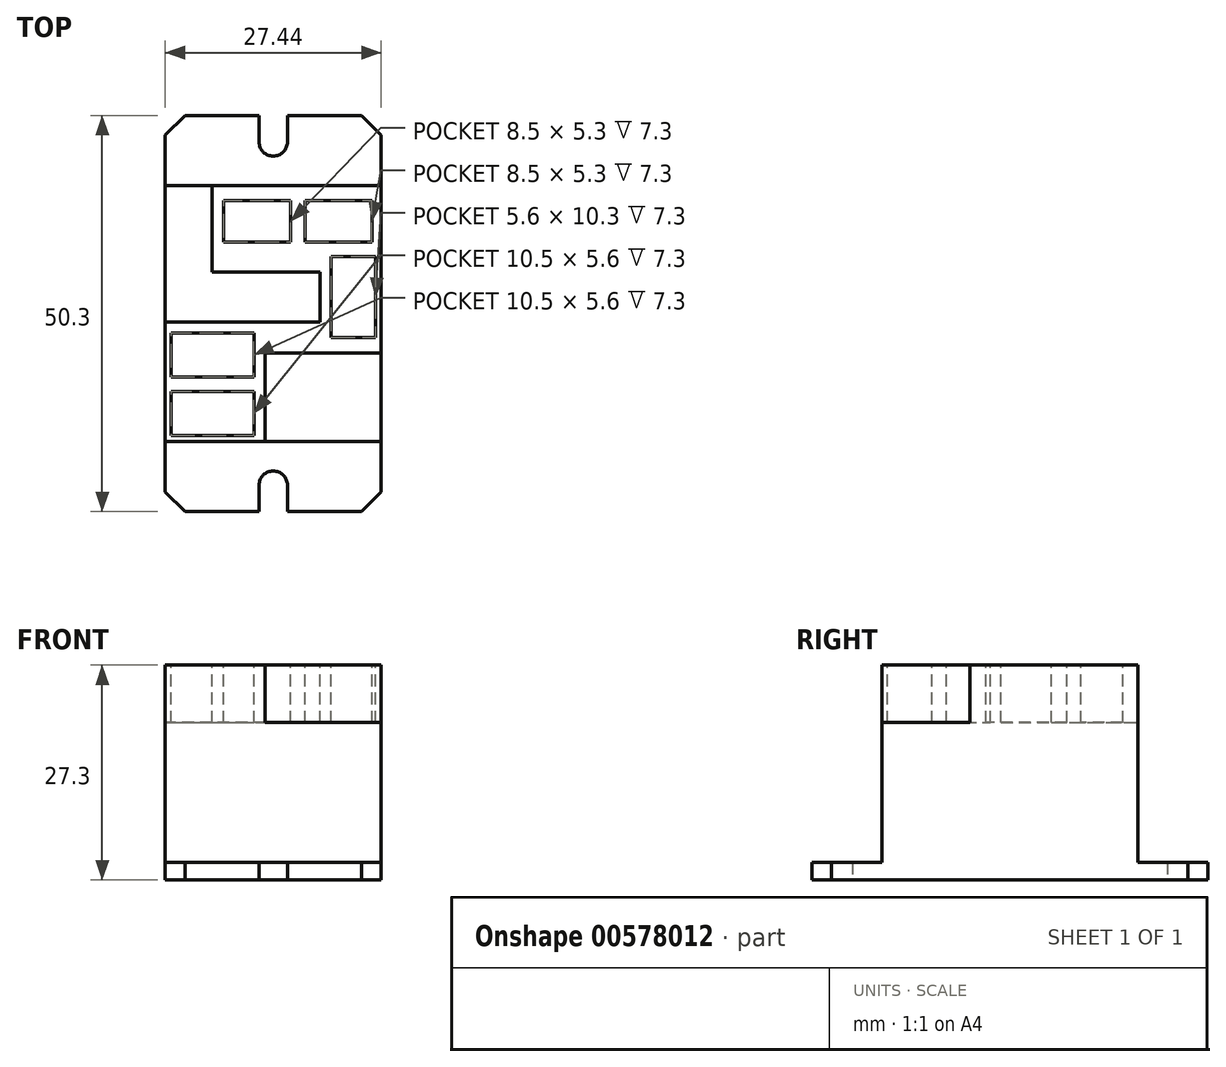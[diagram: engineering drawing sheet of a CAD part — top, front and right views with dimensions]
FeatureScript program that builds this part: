
annotation { "Feature Type Name" : "Feature", "Feature Type Description" : "" }
export const myFeature = defineFeature(function(context is Context, id is Id, definition is map)
    precondition{}
    {
        {
            var Q0;
            Q0=qCreatedBy(makeId("Top.planeOp"),FACE);
            var sketch = newSketch(context, id + "F0", { "sketchPlane" : qUnion([Q0])});
            skLineSegment(sketch, "E0.bottom", {"start": v(13.72, -25.15) * mm, "end": v(-13.72, -25.15) * mm});
            skLineSegment(sketch, "E0.top", {"start": v(13.72, 25.15) * mm, "end": v(-13.72, 25.15) * mm});
            skLineSegment(sketch, "E0.left", {"start": v(13.72, -25.15) * mm, "end": v(13.72, 25.15) * mm});
            skLineSegment(sketch, "E0.right", {"start": v(-13.72, -25.15) * mm, "end": v(-13.72, 25.15) * mm});
            skPoint(sketch, "E0.middle", {"position": v(0, 0) * mm});
            skLineSegment(sketch, "E1.bottom", {"start": v(13.72, -16.26) * mm, "end": v(-13.72, -16.26) * mm});
            skLineSegment(sketch, "E1.top", {"start": v(13.72, 16.26) * mm, "end": v(-13.72, 16.26) * mm});
            skLineSegment(sketch, "E1.left", {"start": v(13.72, -16.26) * mm, "end": v(13.72, 16.26) * mm});
            skLineSegment(sketch, "E1.right", {"start": v(-13.72, -16.26) * mm, "end": v(-13.72, 16.26) * mm});
            skSolve(sketch);
        }
        {
            var Q0;
            Q0=makeQuery(id+"F0.imprint","IMPRINT",FACE,{"disambiguationData":[TD([[makeQuery(id+"F0.imprint","IMPRINT",EDGE,{"derivedFrom":sQuery(id+"F0.wireOp",EDGE,"E1.bottom")}),-1.0]])]});
            extrude(context, id + "F1", {"entities" : qUnion([Q0]), "depth" : 27.3 * mm, "offsetDistance" : 25 * mm});
        }
        {
            var Q0;
            {var subQ0=sQuery(id+"F0.wireOp",EDGE,"E0.top");Q0=makeQuery(id+"F0.imprint","IMPRINT",FACE,{"disambiguationData":[TD([[makeQuery(id+"F0.imprint","IMPRINT",EDGE,{"derivedFrom":subQ0}),1.0]])]});}
            var Q1;
            {var subQ0=sQuery(id+"F0.wireOp",EDGE,"E0.bottom");Q1=makeQuery(id+"F0.imprint","IMPRINT",FACE,{"disambiguationData":[TD([[makeQuery(id+"F0.imprint","IMPRINT",EDGE,{"derivedFrom":subQ0}),-1.0]])]});}
            extrude(context, id + "F2", {"entities" : qUnion([Q0, Q1]), "operationType" : NewBodyOperationType.ADD, "depth" : 2.2 * mm, "offsetDistance" : 25 * mm});
        }
        {
            var Q0;
            Q0=makeQuery(id+"F2.opExtrude","SWEPT_EDGE",EDGE,{"disambiguationData":[OSD([sQuery(id+"F0.wireOp",EDGE,"E0.bottom"),sQuery(id+"F0.wireOp",EDGE,"E0.right")])]});
            var Q1;
            Q1=makeQuery(id+"F2.opExtrude","SWEPT_EDGE",EDGE,{"disambiguationData":[OSD([sQuery(id+"F0.wireOp",EDGE,"E0.bottom"),sQuery(id+"F0.wireOp",EDGE,"E0.left")])]});
            var Q2;
            Q2=makeQuery(id+"F2.opExtrude","SWEPT_EDGE",EDGE,{"disambiguationData":[OSD([sQuery(id+"F0.wireOp",EDGE,"E0.top"),sQuery(id+"F0.wireOp",EDGE,"E0.left")])]});
            var Q3;
            Q3=makeQuery(id+"F2.opExtrude","SWEPT_EDGE",EDGE,{"disambiguationData":[OSD([sQuery(id+"F0.wireOp",EDGE,"E0.top"),sQuery(id+"F0.wireOp",EDGE,"E0.right")])]});
            chamfer(context, id + "F3", {"entities" : qUnion([Q0, Q1, Q2, Q3]), "width" : 2.5 * mm, "tangentPropagation" : true});
        }
        {
            var Q0;
            Q0=makeQuery(id+"F1.opExtrude","CAP_FACE",FACE,{"disambiguationData":[OSD([sQuery(id+"F0.wireOp",EDGE,"E1.bottom"),sQuery(id+"F0.wireOp",EDGE,"E1.top"),sQuery(id+"F0.wireOp",EDGE,"E1.left"),sQuery(id+"F0.wireOp",EDGE,"E1.right")])],"isStart":false});
            var sketch = newSketch(context, id + "F4", { "sketchPlane" : qUnion([Q0])});
            skLineSegment(sketch, "E2.bottom", {"start": v(13.72, -16.26) * mm, "end": v(-1.02, -16.26) * mm});
            skLineSegment(sketch, "E2.top", {"start": v(13.72, -5.04) * mm, "end": v(-1.02, -5.04) * mm});
            skLineSegment(sketch, "E2.left", {"start": v(13.72, -16.26) * mm, "end": v(13.72, -5.04) * mm});
            skLineSegment(sketch, "E2.right", {"start": v(-1.02, -16.26) * mm, "end": v(-1.02, -5.04) * mm});
            skLineSegment(sketch, "E3", {"start": v(-13.72, 16.26) * mm, "end": v(-13.72, -1.1) * mm});
            skLineSegment(sketch, "E4", {"start": v(-13.72, -1.1) * mm, "end": v(5.92, -1.1) * mm});
            skLineSegment(sketch, "E5", {"start": v(5.92, -1.1) * mm, "end": v(5.92, 5.3) * mm});
            skLineSegment(sketch, "E6", {"start": v(5.92, 5.3) * mm, "end": v(-7.78, 5.3) * mm});
            skLineSegment(sketch, "E7", {"start": v(-7.78, 5.3) * mm, "end": v(-7.78, 16.26) * mm});
            skLineSegment(sketch, "E8", {"start": v(-7.78, 16.26) * mm, "end": v(-13.72, 16.26) * mm});
            skSolve(sketch);
        }
        {
            var Q0;
            Q0=makeQuery(id+"F4.imprint","IMPRINT",FACE,{"disambiguationData":[TD([[makeQuery(id+"F4.imprint","IMPRINT",EDGE,{"derivedFrom":sQuery(id+"F4.wireOp",EDGE,"E2.bottom")}),-1.0]])]});
            var Q1;
            Q1=makeQuery(id+"F4.imprint","IMPRINT",FACE,{"disambiguationData":[TD([[makeQuery(id+"F4.imprint","IMPRINT",EDGE,{"derivedFrom":sQuery(id+"F4.wireOp",EDGE,"E3")}),-1.0]])]});
            extrude(context, id + "F5", {"entities" : qUnion([Q0, Q1]), "operationType" : NewBodyOperationType.REMOVE, "oppositeDirection" : true, "depth" : 7.3 * mm, "offsetDistance" : 25 * mm});
        }
        {
            var Q0;
            Q0=makeQuery(id+"F1.opExtrude","CAP_FACE",FACE,{"disambiguationData":[OSD([sQuery(id+"F0.wireOp",EDGE,"E1.bottom"),sQuery(id+"F0.wireOp",EDGE,"E1.top"),sQuery(id+"F0.wireOp",EDGE,"E1.left"),sQuery(id+"F0.wireOp",EDGE,"E1.right")])],"isStart":false});
            var sketch = newSketch(context, id + "F6", { "sketchPlane" : qUnion([Q0])});
            skLineSegment(sketch, "E9", {"start": v(-7.78, 14.36) * mm, "end": v(13.72, 14.36) * mm, "construction": true});
            skLineSegment(sketch, "E10.bottom", {"start": v(-6.28, 14.36) * mm, "end": v(2.22, 14.36) * mm});
            skLineSegment(sketch, "E10.top", {"start": v(-6.28, 9.06) * mm, "end": v(2.22, 9.06) * mm});
            skLineSegment(sketch, "E10.left", {"start": v(-6.28, 14.36) * mm, "end": v(-6.28, 9.06) * mm});
            skLineSegment(sketch, "E10.right", {"start": v(2.22, 14.36) * mm, "end": v(2.22, 9.06) * mm});
            skLineSegment(sketch, "E11", {"start": v(3.12, 14.36) * mm, "end": v(3.12, 8.09) * mm, "construction": true});
            skLineSegment(sketch, "E12.MirrorCS", {"start": v(4.02, 14.36) * mm, "end": v(4.02, 9.06) * mm});
            skLineSegment(sketch, "E13.MirrorCS", {"start": v(12.52, 9.06) * mm, "end": v(4.02, 9.06) * mm});
            skLineSegment(sketch, "E14.MirrorCS", {"start": v(12.52, 14.36) * mm, "end": v(12.52, 9.06) * mm});
            skLineSegment(sketch, "E15", {"start": v(4.02, 14.36) * mm, "end": v(12.52, 14.36) * mm});
            skLineSegment(sketch, "E16", {"start": v(13.72, 7.26) * mm, "end": v(5.76, 7.26) * mm, "construction": true});
            skLineSegment(sketch, "E17", {"start": v(12.97, 7.26) * mm, "end": v(12.97, -5.04) * mm, "construction": true});
            skLineSegment(sketch, "E18.bottom", {"start": v(12.97, 7.26) * mm, "end": v(7.37, 7.26) * mm});
            skLineSegment(sketch, "E18.top", {"start": v(12.97, -3.04) * mm, "end": v(7.37, -3.04) * mm});
            skLineSegment(sketch, "E18.left", {"start": v(12.97, 7.26) * mm, "end": v(12.97, -3.04) * mm});
            skLineSegment(sketch, "E18.right", {"start": v(7.37, 7.26) * mm, "end": v(7.37, -3.04) * mm});
            skLineSegment(sketch, "E19", {"start": v(-12.97, -16.26) * mm, "end": v(-12.97, -1.1) * mm, "construction": true});
            skLineSegment(sketch, "E20", {"start": v(-12.97, -15.5) * mm, "end": v(-1.02, -15.5) * mm, "construction": true});
            skLineSegment(sketch, "E21.bottom", {"start": v(-12.97, -15.5) * mm, "end": v(-2.47, -15.5) * mm});
            skLineSegment(sketch, "E21.top", {"start": v(-12.97, -9.9) * mm, "end": v(-2.47, -9.9) * mm});
            skLineSegment(sketch, "E21.left", {"start": v(-12.97, -15.5) * mm, "end": v(-12.97, -9.9) * mm});
            skLineSegment(sketch, "E21.right", {"start": v(-2.47, -15.5) * mm, "end": v(-2.47, -9.9) * mm});
            skLineSegment(sketch, "E22.bottom", {"start": v(-12.97, -8.06) * mm, "end": v(-2.47, -8.06) * mm});
            skLineSegment(sketch, "E22.top", {"start": v(-12.97, -2.46) * mm, "end": v(-2.47, -2.46) * mm});
            skLineSegment(sketch, "E22.left", {"start": v(-12.97, -8.06) * mm, "end": v(-12.97, -2.46) * mm});
            skLineSegment(sketch, "E22.right", {"start": v(-2.47, -8.06) * mm, "end": v(-2.47, -2.46) * mm});
            skSolve(sketch);
        }
        {
            var Q0;
            Q0 = qSketchRegion(id + "F6", true);
            extrude(context, id + "F7", {"entities" : qUnion([Q0]), "operationType" : NewBodyOperationType.REMOVE, "oppositeDirection" : true, "depth" : 7.3 * mm, "offsetDistance" : 25 * mm});
        }
        {
            var Q0;
            Q0=makeQuery(id+"F0.imprint","IMPRINT",FACE,{"disambiguationData":[TD([[makeQuery(id+"F0.imprint","IMPRINT",EDGE,{"derivedFrom":sQuery(id+"F0.wireOp",EDGE,"E1.bottom")}),-1.0]])]});
            var sketch = newSketch(context, id + "F8", { "sketchPlane" : qUnion([Q0])});
            skPoint(sketch, "E23", {"position": v(0, -20) * mm});
            skPoint(sketch, "E24", {"position": v(0, 20) * mm});
            skLineSegment(sketch, "E25.bottom", {"start": v(0, -20) * mm, "end": v(0, -20) * mm});
            skLineSegment(sketch, "E25.top", {"start": v(0, -25.15) * mm, "end": v(-1.8, -25.15) * mm});
            skLineSegment(sketch, "E25.left", {"start": v(0, -20) * mm, "end": v(0, -25.15) * mm, "construction": true});
            skLineSegment(sketch, "E25.right", {"start": v(-1.8, -21.8) * mm, "end": v(-1.8, -25.15) * mm});
            skPoint(sketch, "E26.visualSharp", {"position": v(-1.8, -20) * mm});
            skArc(sketch, "E26.filletArc", {"start": v(0, -20) * mm, "mid": v(-1.27, -20.53) * mm, "end": v(-1.8, -21.8) * mm});
            skLineSegment(sketch, "E27.MirrorCS", {"start": v(0, -25.15) * mm, "end": v(1.8, -25.15) * mm});
            skLineSegment(sketch, "E28.MirrorCS", {"start": v(1.8, -21.8) * mm, "end": v(1.8, -25.15) * mm});
            skArc(sketch, "E29.MirrorCS", {"start": v(0, -20) * mm, "mid": v(1.27, -20.53) * mm, "end": v(1.8, -21.8) * mm});
            skLineSegment(sketch, "E30.MirrorCS", {"start": v(0, 25.15) * mm, "end": v(1.8, 25.15) * mm});
            skLineSegment(sketch, "E31.MirrorCS", {"start": v(0, 25.15) * mm, "end": v(-1.8, 25.15) * mm});
            skLineSegment(sketch, "E32.MirrorCS", {"start": v(-1.8, 21.8) * mm, "end": v(-1.8, 25.15) * mm});
            skArc(sketch, "E33.MirrorCS", {"start": v(0, 20) * mm, "mid": v(-1.27, 20.53) * mm, "end": v(-1.8, 21.8) * mm});
            skArc(sketch, "E34.MirrorCS", {"start": v(0, 20) * mm, "mid": v(1.27, 20.53) * mm, "end": v(1.8, 21.8) * mm});
            skLineSegment(sketch, "E35.MirrorCS", {"start": v(1.8, 21.8) * mm, "end": v(1.8, 25.15) * mm});
            skSolve(sketch);
        }
        {
            var Q0;
            Q0 = qSketchRegion(id + "F8", true);
            extrude(context, id + "F9", {"entities" : qUnion([Q0]), "operationType" : NewBodyOperationType.REMOVE, "endBound" : BoundingType.THROUGH_ALL, "depth" : 25 * mm, "offsetDistance" : 25 * mm});
        }
    });
